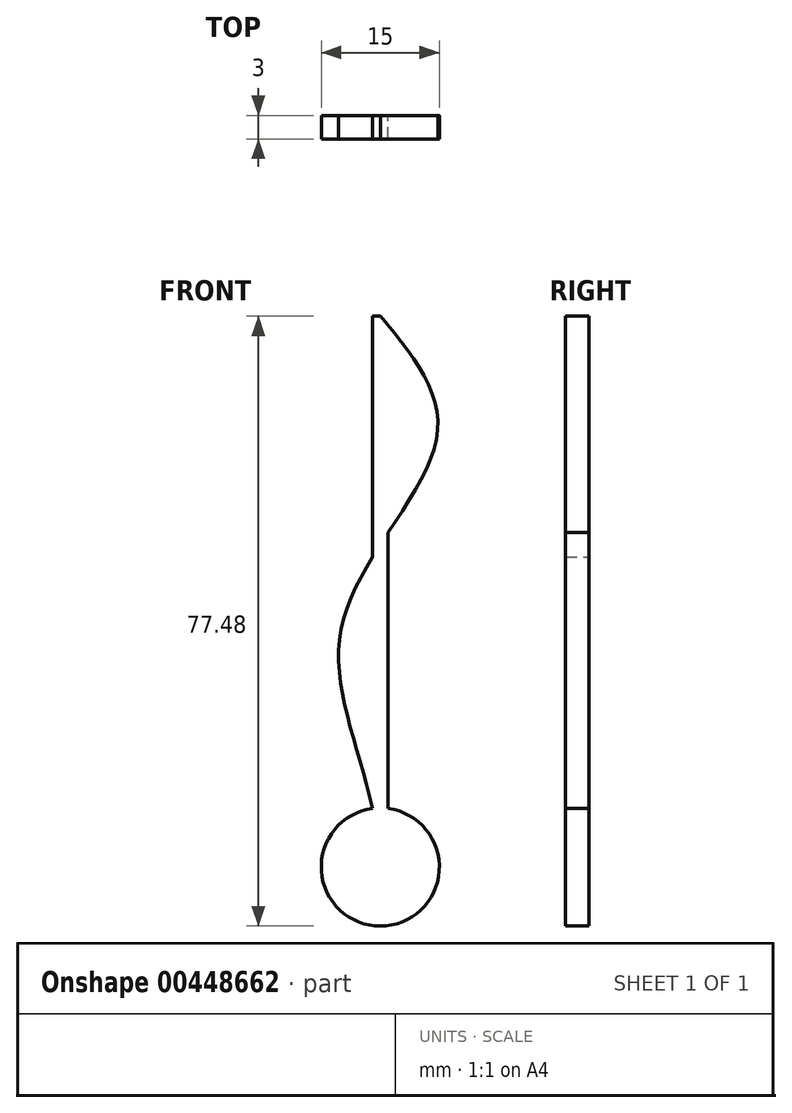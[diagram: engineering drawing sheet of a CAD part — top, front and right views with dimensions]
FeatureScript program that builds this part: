
annotation { "Feature Type Name" : "Feature", "Feature Type Description" : "" }
export const myFeature = defineFeature(function(context is Context, id is Id, definition is map)
    precondition{}
    {
        {
            var Q0;
            Q0=qCreatedBy(makeId("Front.planeOp"),FACE);
            var sketch = newSketch(context, id + "F0", { "sketchPlane" : qUnion([Q0])});
            skCircle(sketch, "E0", {"center": v(0, 0) * mm, "radius": 7.5 * mm});
            skFitSpline(sketch, "E1", {"points": [v(0, 0) * mm, v(-4.96, 30.32) * mm, v(7.14, 54.33) * mm, v(0, 69.98) * mm], "startDerivative": vector(-2.8, 91.6) * mm, "endDerivative": vector(-46, 53.65) * mm});
            skLineSegment(sketch, "E2", {"start": v(1, 42.5) * mm, "end": v(1, 7.43) * mm});
            skLineSegment(sketch, "E3", {"start": v(-1, 39.36) * mm, "end": v(-1, 69.98) * mm});
            skLineSegment(sketch, "E4", {"start": v(1, 0) * mm, "end": v(0, 0) * mm, "construction": true});
            skLineSegment(sketch, "E5", {"start": v(0, 0) * mm, "end": v(-1, 0) * mm, "construction": true});
            skLineSegment(sketch, "E6", {"start": v(0, 69.98) * mm, "end": v(-1, 69.98) * mm});
            skPoint(sketch, "E7.orphan", {"position": v(1, 69.98) * mm});
            skSolve(sketch);
        }
        {
            var Q0;
            Q0 = qSketchRegion(id + "F0", true);
            extrude(context, id + "F1", {"entities" : qUnion([Q0]), "depth" : 3 * mm});
        }
    });
